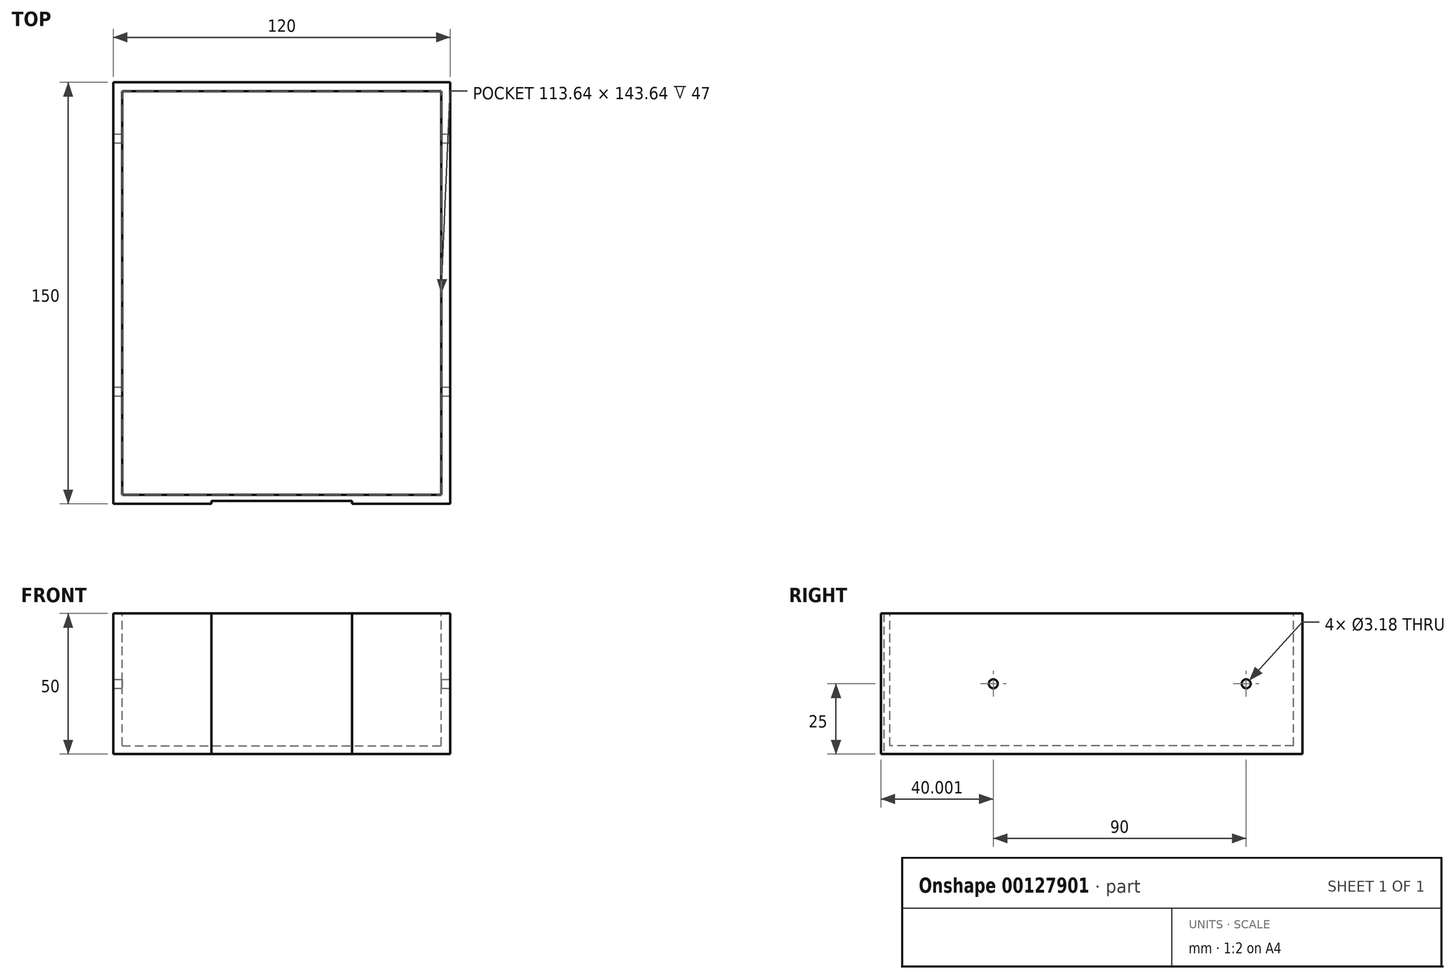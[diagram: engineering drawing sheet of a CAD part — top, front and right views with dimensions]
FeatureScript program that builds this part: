
annotation { "Feature Type Name" : "Feature", "Feature Type Description" : "" }
export const myFeature = defineFeature(function(context is Context, id is Id, definition is map)
    precondition{}
    {
        {
            var Q0;
            Q0=qCreatedBy(makeId("Top.planeOp"),FACE);
            var sketch = newSketch(context, id + "F0", { "sketchPlane" : qUnion([Q0])});
            skLineSegment(sketch, "E0.bottom", {"start": v(-70.06, 114.81) * mm, "end": v(49.94, 114.81) * mm});
            skLineSegment(sketch, "E0.top", {"start": v(-70.06, -35.19) * mm, "end": v(49.94, -35.19) * mm});
            skLineSegment(sketch, "E0.left", {"start": v(-70.06, 114.81) * mm, "end": v(-70.06, -35.19) * mm});
            skLineSegment(sketch, "E0.right", {"start": v(49.94, 114.81) * mm, "end": v(49.94, -35.19) * mm});
            skLineSegment(sketch, "E1", {"start": v(-66.88, 114.81) * mm, "end": v(-66.88, -35.19) * mm});
            skLineSegment(sketch, "E2", {"start": v(46.76, -35.19) * mm, "end": v(46.76, 114.81) * mm});
            skLineSegment(sketch, "E3", {"start": v(-70.06, 111.63) * mm, "end": v(49.94, 111.63) * mm});
            skLineSegment(sketch, "E4", {"start": v(-70.06, -32) * mm, "end": v(49.94, -32) * mm});
            skSolve(sketch);
        }
        {
            var Q0;
            {var subQ0=sQuery(id+"F0.wireOp",EDGE,"E1");var subQ1=sQuery(id+"F0.wireOp",EDGE,"E0.bottom");var subQ2=makeQuery(id+"F0.imprint","INTERSECT",VERTEX,{"derivedFrom":[subQ1,subQ0]});Q0=makeQuery(id+"F0.imprint","IMPRINT",FACE,{"disambiguationData":[TD([[makeQuery(id+"F0.imprint","IMPRINT",EDGE,{"disambiguationData":[TD([[subQ2,-1.0]])],"derivedFrom":subQ1}),-1.0]])]});}
            var Q1;
            {var subQ0=sQuery(id+"F0.wireOp",EDGE,"E0.left");var subQ1=sQuery(id+"F0.wireOp",EDGE,"E0.bottom");var subQ2=makeQuery(id+"F0.imprint","INTERSECT",VERTEX,{"derivedFrom":[subQ1,subQ0]});Q1=makeQuery(id+"F0.imprint","IMPRINT",FACE,{"disambiguationData":[TD([[makeQuery(id+"F0.imprint","IMPRINT",EDGE,{"disambiguationData":[TD([[subQ2,-1.0]])],"derivedFrom":subQ1}),-1.0]])]});}
            var Q2;
            {var subQ0=sQuery(id+"F0.wireOp",EDGE,"E3");var subQ1=sQuery(id+"F0.wireOp",EDGE,"E0.left");var subQ2=makeQuery(id+"F0.imprint","INTERSECT",VERTEX,{"derivedFrom":[subQ1,subQ0]});Q2=makeQuery(id+"F0.imprint","IMPRINT",FACE,{"disambiguationData":[TD([[makeQuery(id+"F0.imprint","IMPRINT",EDGE,{"disambiguationData":[TD([[subQ2,-1.0]])],"derivedFrom":subQ1}),1.0]])]});}
            var Q3;
            {var subQ0=sQuery(id+"F0.wireOp",EDGE,"E1");var subQ1=sQuery(id+"F0.wireOp",EDGE,"E0.top");var subQ2=makeQuery(id+"F0.imprint","INTERSECT",VERTEX,{"derivedFrom":[subQ1,subQ0]});Q3=makeQuery(id+"F0.imprint","IMPRINT",FACE,{"disambiguationData":[TD([[makeQuery(id+"F0.imprint","IMPRINT",EDGE,{"disambiguationData":[TD([[subQ2,-1.0]])],"derivedFrom":subQ1}),1.0]])]});}
            var Q4;
            {var subQ0=sQuery(id+"F0.wireOp",EDGE,"E3");var subQ1=sQuery(id+"F0.wireOp",EDGE,"E0.right");var subQ2=makeQuery(id+"F0.imprint","INTERSECT",VERTEX,{"derivedFrom":[subQ1,subQ0]});Q4=makeQuery(id+"F0.imprint","IMPRINT",FACE,{"disambiguationData":[TD([[makeQuery(id+"F0.imprint","IMPRINT",EDGE,{"disambiguationData":[TD([[subQ2,-1.0]])],"derivedFrom":subQ1}),-1.0]])]});}
            var Q5;
            {var subQ0=sQuery(id+"F0.wireOp",EDGE,"E0.right");var subQ1=sQuery(id+"F0.wireOp",EDGE,"E0.top");var subQ2=makeQuery(id+"F0.imprint","INTERSECT",VERTEX,{"derivedFrom":[subQ1,subQ0]});Q5=makeQuery(id+"F0.imprint","IMPRINT",FACE,{"disambiguationData":[TD([[makeQuery(id+"F0.imprint","IMPRINT",EDGE,{"disambiguationData":[TD([[subQ2,1.0]])],"derivedFrom":subQ1}),1.0]])]});}
            var Q6;
            {var subQ0=sQuery(id+"F0.wireOp",EDGE,"E0.right");var subQ1=sQuery(id+"F0.wireOp",EDGE,"E0.bottom");var subQ2=makeQuery(id+"F0.imprint","INTERSECT",VERTEX,{"derivedFrom":[subQ1,subQ0]});Q6=makeQuery(id+"F0.imprint","IMPRINT",FACE,{"disambiguationData":[TD([[makeQuery(id+"F0.imprint","IMPRINT",EDGE,{"disambiguationData":[TD([[subQ2,1.0]])],"derivedFrom":subQ1}),-1.0]])]});}
            var Q7;
            {var subQ0=sQuery(id+"F0.wireOp",EDGE,"E0.left");var subQ1=sQuery(id+"F0.wireOp",EDGE,"E0.top");var subQ2=makeQuery(id+"F0.imprint","INTERSECT",VERTEX,{"derivedFrom":[subQ1,subQ0]});Q7=makeQuery(id+"F0.imprint","IMPRINT",FACE,{"disambiguationData":[TD([[makeQuery(id+"F0.imprint","IMPRINT",EDGE,{"disambiguationData":[TD([[subQ2,-1.0]])],"derivedFrom":subQ1}),1.0]])]});}
            var Q8;
            {var subQ0=sQuery(id+"F0.wireOp",EDGE,"E3");var subQ1=sQuery(id+"F0.wireOp",EDGE,"E1");var subQ2=makeQuery(id+"F0.imprint","INTERSECT",VERTEX,{"derivedFrom":[subQ1,subQ0]});Q8=makeQuery(id+"F0.imprint","IMPRINT",FACE,{"disambiguationData":[TD([[makeQuery(id+"F0.imprint","IMPRINT",EDGE,{"disambiguationData":[TD([[subQ2,-1.0]])],"derivedFrom":subQ1}),1.0]])]});}
            extrude(context, id + "F1", {"entities" : qUnion([Q0, Q1, Q2, Q3, Q4, Q5, Q6, Q7, Q8]), "depth" : 50 * mm});
        }
        {
            var Q0;
            Q0=makeQuery(id+"F1.opExtrude","CAP_FACE",FACE,{"disambiguationData":[OSD([sQuery(id+"F0.wireOp",EDGE,"E0.bottom"),sQuery(id+"F0.wireOp",EDGE,"E0.top"),sQuery(id+"F0.wireOp",EDGE,"E0.left"),sQuery(id+"F0.wireOp",EDGE,"E0.right")])],"isStart":false});
            var sketch = newSketch(context, id + "F2", { "sketchPlane" : qUnion([Q0])});
            skLineSegment(sketch, "E5", {"start": v(-70.06, 111.63) * mm, "end": v(49.94, 111.63) * mm});
            skLineSegment(sketch, "E6", {"start": v(-70.06, -32) * mm, "end": v(49.94, -32) * mm});
            skLineSegment(sketch, "E7", {"start": v(46.76, -35.19) * mm, "end": v(46.76, 114.81) * mm});
            skLineSegment(sketch, "E8", {"start": v(-66.88, 114.81) * mm, "end": v(-66.88, -35.19) * mm});
            skSolve(sketch);
        }
        {
            var Q0;
            {var subQ0=sQuery(id+"F2.wireOp",EDGE,"E8");var subQ1=sQuery(id+"F2.wireOp",EDGE,"E5");var subQ2=makeQuery(id+"F2.imprint","INTERSECT",VERTEX,{"derivedFrom":[subQ1,subQ0]});Q0=makeQuery(id+"F2.imprint","IMPRINT",FACE,{"disambiguationData":[TD([[makeQuery(id+"F2.imprint","IMPRINT",EDGE,{"disambiguationData":[TD([[subQ2,-1.0]])],"derivedFrom":subQ1}),-1.0]])]});}
            extrude(context, id + "F3", {"entities" : qUnion([Q0]), "operationType" : NewBodyOperationType.REMOVE, "oppositeDirection" : true, "depth" : 47 * mm});
        }
        {
            var Q0;
            Q0=makeQuery(id+"F1.opExtrude","SWEPT_FACE",FACE,{"disambiguationData":[OSD([sQuery(id+"F0.wireOp",EDGE,"E0.right")])]});
            var sketch = newSketch(context, id + "F4", { "sketchPlane" : qUnion([Q0])});
            skLineSegment(sketch, "E9", {"start": v(4.81, 50) * mm, "end": v(4.81, 0) * mm});
            skLineSegment(sketch, "E10", {"start": v(94.81, 50) * mm, "end": v(94.81, 0) * mm});
            skCircle(sketch, "E11", {"center": v(4.81, 25) * mm, "radius": 1.6 * mm});
            skCircle(sketch, "E12", {"center": v(94.81, 25) * mm, "radius": 1.6 * mm});
            skSolve(sketch);
        }
        {
            var Q0;
            Q0 = qSketchRegion(id + "F4", true);
            extrude(context, id + "F5", {"entities" : qUnion([Q0]), "operationType" : NewBodyOperationType.REMOVE, "endBound" : BoundingType.THROUGH_ALL, "oppositeDirection" : true, "depth" : 100 * mm});
        }
        {
            var Q0;
            Q0=makeQuery(id+"F1.opExtrude","SWEPT_FACE",FACE,{"disambiguationData":[OSD([sQuery(id+"F0.wireOp",EDGE,"E0.top")])]});
            var sketch = newSketch(context, id + "F6", { "sketchPlane" : qUnion([Q0])});
            skLineSegment(sketch, "E13", {"start": v(-35.06, 50) * mm, "end": v(-35.06, 0) * mm});
            skLineSegment(sketch, "E14", {"start": v(14.94, 50) * mm, "end": v(14.94, 0) * mm});
            skLineSegment(sketch, "E15", {"start": v(-35.06, 50) * mm, "end": v(14.94, 50) * mm});
            skLineSegment(sketch, "E16", {"start": v(14.94, 0) * mm, "end": v(-35.06, 0) * mm});
            skSolve(sketch);
        }
        {
            var Q0;
            Q0 = qSketchRegion(id + "F6", true);
            extrude(context, id + "F7", {"entities" : qUnion([Q0]), "operationType" : NewBodyOperationType.REMOVE, "oppositeDirection" : true, "depth" : 1 * mm});
        }
    });
